# Revit family: Холодильные шкафы POLAIR BAKERY
name_source: partatom
category: Оборудование
units: mm (PartAtom-declared; Revit-internal decimal feet)

## family parameters
Всегда вертикально = Да
Классификация = Нет
На основе рабочей плоскости = Нет
Общий = Нет
При загрузке вырезать с полостями = Нет
Размер круглого соединителя = Использовать диаметр
Тип детали = Нормальный
Точка расчета площади = Нет

## types (2) — shared parameters
Вес нетто/брутто, кг = 165/190
Высота = 1960 мм
Габаритные размеры, мм = 697*1005*1960
Глубина = 1005 мм
Диап. рабочих темп. = -10....+40
Корпус = цельнозаливной
Направляющие под EN 40*60 = 20 пар
Объем, л = 700
Педаль = +
Размеры в упаковке, мм = 790x1080x2125
Регул. уровня влажности, % = от 60 до 95
Система электропитания, В/Гц = 230/50
Темп. окр. среды = от +12 до +40
Тип оттайки = автоматическая
Холодильный шкаф = <По категории>
Ширина = 697 мм
zero-valued in all types: Отметка по умолчанию

## per-type parameters (varying)
| type | Цена, руб. | Экран 5 дюймов | Экран 7 дюймов |
| CS107 Bakery Br (тип 1 с дисплеем 5) | 204 900 | Да | Нет |
| CS107-Bakery Br (тип 2 с дисплеем 7) | 229 900 | Нет | Да |
